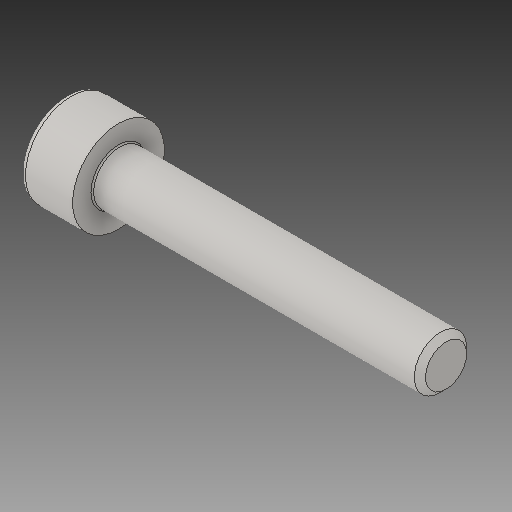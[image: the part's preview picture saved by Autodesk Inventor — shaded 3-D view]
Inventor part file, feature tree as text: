
AUTODESK INVENTOR PART (.ipt)
format: ipt  version: 2019 (Build 230136000, 136)  size: 129,536 bytes
history: imported  units: mm
features: imported_body x1
ambient origin geometry x8: Origin, YZ Plane, XZ Plane, XY Plane, X Axis, Y Axis, Z Axis, Center Point
bodies: Solide1 (imported_parasolid), Solid1 (imported_parasolid)
feature tree (1):
  imported_body  NMx_Import_Brep_tag  [imported B-rep: ~6 faces, bbox_mm=None]
